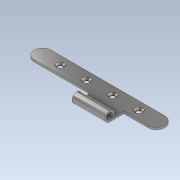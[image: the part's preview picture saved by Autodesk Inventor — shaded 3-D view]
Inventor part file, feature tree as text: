
AUTODESK INVENTOR PART (.ipt)
format: ipt  version: 2021 (Build 250183000, 183)  size: 152,576 bytes
history: native  units: mm
features: sketch x4, extrude x3, fillet x3, other x1, hole x1, chamfer x1, projected_geometry x1
ambient origin geometry x8: Origin, YZ Plane, XZ Plane, XY Plane, X Axis, Y Axis, Z Axis, Center Point
bodies: Body1 (feature_tree)
feature tree (14):
  other  "Sólido1"
  extrude  "Extrusión1"  Depth=2.5mm TaperAngle=0.0deg
  extrude  "Extrusión2"  Depth=40.0mm
  extrude  "Extrusión3"  Depth=40.0mm
  hole  "Agujero1"  [1 undecoded]
  chamfer  "Chaflán1"  Distance=2.5mm
  fillet  "Empalme2"  Radius=32.0mm
  fillet  "Empalme3"  Radius=32.0mm
  fillet  "Empalme6"  Radius=32.0mm
  sketch  "Boceto2"  dims[d2=20.5mm d3=2.5mm d4=0.0mm]
  sketch  "Boceto3"  dims[d5=40.0mm d6=12.5mm]
  sketch  "Boceto4"  dims[d7=40.0mm d8=12.0mm]
  projected_geometry  "Contorno proyectado1"
  sketch  "Boceto5"  dims[d9=2.0mm d10=2.5mm d11=0.0mm d12=2.5mm d13=0.0mm d14=32.0mm d15=32.0mm d18=32.0mm d19=32.0mm d20=5.5mm d21=6.0mm d22=4.0mm d23=2.0mm d24=90.0deg d25=8.0mm d26=20.594885mm d27=2.0mm d28=2.0mm d29=45.0deg d33=5.0mm]
note: 1 required parameter value undecoded (feature->parameter linkage not recoverable at this tier; creation-order binding heuristic only, values carry confidence <= 0.55)
